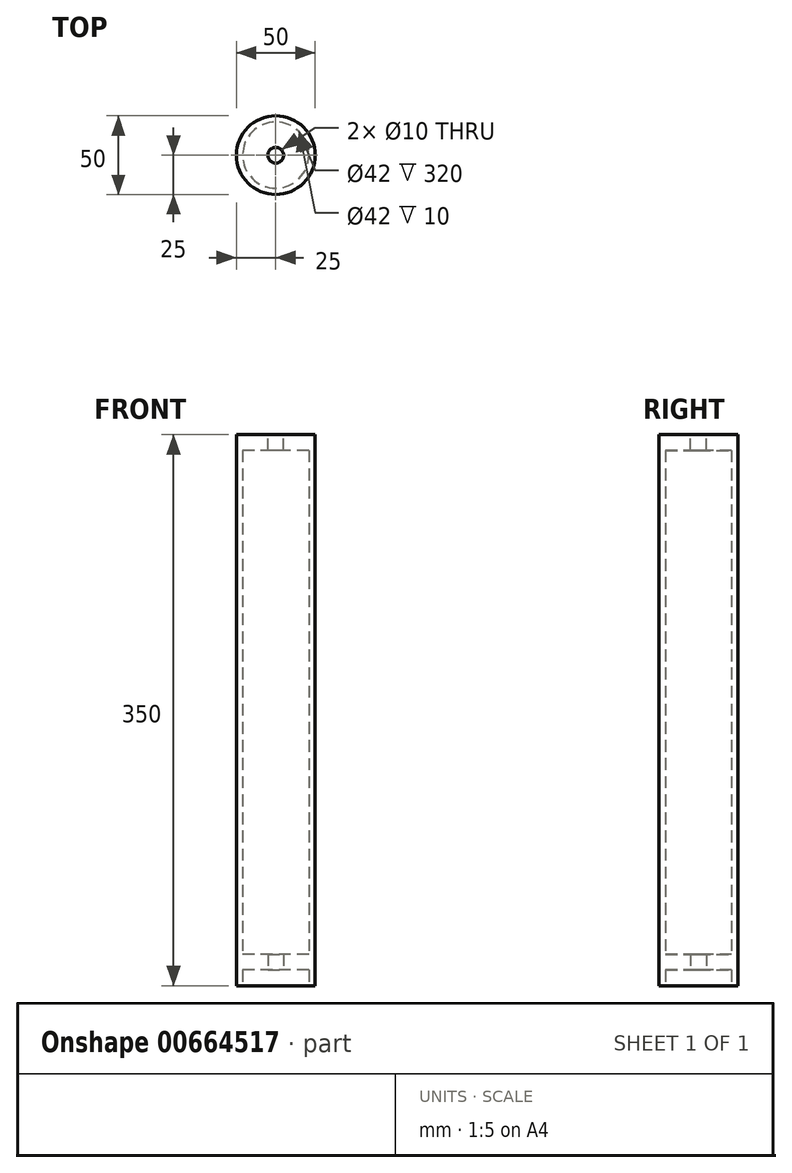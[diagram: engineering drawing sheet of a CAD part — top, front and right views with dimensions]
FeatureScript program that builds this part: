
annotation { "Feature Type Name" : "Feature", "Feature Type Description" : "" }
export const myFeature = defineFeature(function(context is Context, id is Id, definition is map)
    precondition{}
    {
        {
            var Q0;
            Q0=qCreatedBy(makeId("Top.planeOp"),FACE);
            var sketch = newSketch(context, id + "F0", { "sketchPlane" : qUnion([Q0])});
            skCircle(sketch, "E0", {"center": v(0, 0) * mm, "radius": 21 * mm});
            skCircle(sketch, "E1", {"center": v(0, 0) * mm, "radius": 25 * mm});
            skSolve(sketch);
        }
        {
            var Q0;
            Q0=makeQuery(id+"F0.imprint","IMPRINT",FACE,{"disambiguationData":[TD([[makeQuery(id+"F0.imprint","IMPRINT",EDGE,{"derivedFrom":sQuery(id+"F0.wireOp",EDGE,"E0")}),-1.0]])]});
            extrude(context, id + "F1", {"entities" : qUnion([Q0]), "depth" : 10 * mm, "offsetDistance" : 25 * mm});
        }
        {
            var Q0;
            Q0=makeQuery(id+"F1.opExtrude","CAP_FACE",FACE,{"disambiguationData":[OSD([sQuery(id+"F0.wireOp",EDGE,"E0"),sQuery(id+"F0.wireOp",EDGE,"E1")])],"isStart":false});
            var sketch = newSketch(context, id + "F2", { "sketchPlane" : qUnion([Q0])});
            skCircle(sketch, "E2", {"center": v(0, 0) * mm, "radius": 25 * mm});
            skSolve(sketch);
        }
        {
            var Q0;
            Q0 = qSketchRegion(id + "F2", true);
            extrude(context, id + "F3", {"entities" : qUnion([Q0]), "operationType" : NewBodyOperationType.ADD, "depth" : 10 * mm, "offsetDistance" : 25 * mm});
        }
        {
            var Q0;
            Q0=makeQuery(id+"F3.opExtrude","CAP_FACE",FACE,{"disambiguationData":[OSD([sQuery(id+"F2.wireOp",EDGE,"E2")])],"isStart":false});
            var sketch = newSketch(context, id + "F4", { "sketchPlane" : qUnion([Q0])});
            skCircle(sketch, "E3", {"center": v(0, 0) * mm, "radius": 25 * mm});
            skCircle(sketch, "E4", {"center": v(0, 0) * mm, "radius": 21 * mm});
            skSolve(sketch);
        }
        {
            var Q0;
            Q0 = qSketchRegion(id + "F4", true);
            extrude(context, id + "F5", {"entities" : qUnion([Q0]), "operationType" : NewBodyOperationType.ADD, "depth" : 320 * mm, "offsetDistance" : 25 * mm});
        }
        {
            var Q0;
            Q0=makeQuery(id+"F5.opExtrude","CAP_FACE",FACE,{"disambiguationData":[OSD([sQuery(id+"F4.wireOp",EDGE,"E3"),sQuery(id+"F4.wireOp",EDGE,"E4")])],"isStart":false});
            var sketch = newSketch(context, id + "F6", { "sketchPlane" : qUnion([Q0])});
            skCircle(sketch, "E5", {"center": v(0, 0) * mm, "radius": 25 * mm});
            skSolve(sketch);
        }
        {
            var Q0;
            Q0 = qSketchRegion(id + "F6", true);
            extrude(context, id + "F7", {"entities" : qUnion([Q0]), "operationType" : NewBodyOperationType.ADD, "depth" : 10 * mm, "offsetDistance" : 25 * mm});
        }
        {
            var Q0;
            Q0=makeQuery(id+"F7.opExtrude","CAP_FACE",FACE,{"disambiguationData":[OSD([sQuery(id+"F6.wireOp",EDGE,"E5")])],"isStart":false});
            var sketch = newSketch(context, id + "F8", { "sketchPlane" : qUnion([Q0])});
            skCircle(sketch, "E6", {"center": v(0, 0) * mm, "radius": 5 * mm});
            skSolve(sketch);
        }
        {
            var Q0;
            Q0 = qSketchRegion(id + "F8", true);
            extrude(context, id + "F9", {"entities" : qUnion([Q0]), "operationType" : NewBodyOperationType.REMOVE, "oppositeDirection" : true, "depth" : 10 * mm, "offsetDistance" : 25 * mm});
        }
        {
            var Q0;
            Q0=makeQuery(id+"F3.opExtrude","CAP_FACE",FACE,{"disambiguationData":[OSD([sQuery(id+"F2.wireOp",EDGE,"E2")])],"isStart":true});
            var sketch = newSketch(context, id + "F10", { "sketchPlane" : qUnion([Q0])});
            skCircle(sketch, "E7", {"center": v(0, 0) * mm, "radius": 5 * mm});
            skSolve(sketch);
        }
        {
            var Q0;
            Q0 = qSketchRegion(id + "F10", true);
            extrude(context, id + "F11", {"entities" : qUnion([Q0]), "operationType" : NewBodyOperationType.REMOVE, "oppositeDirection" : true, "depth" : 10 * mm, "offsetDistance" : 25 * mm});
        }
    });
